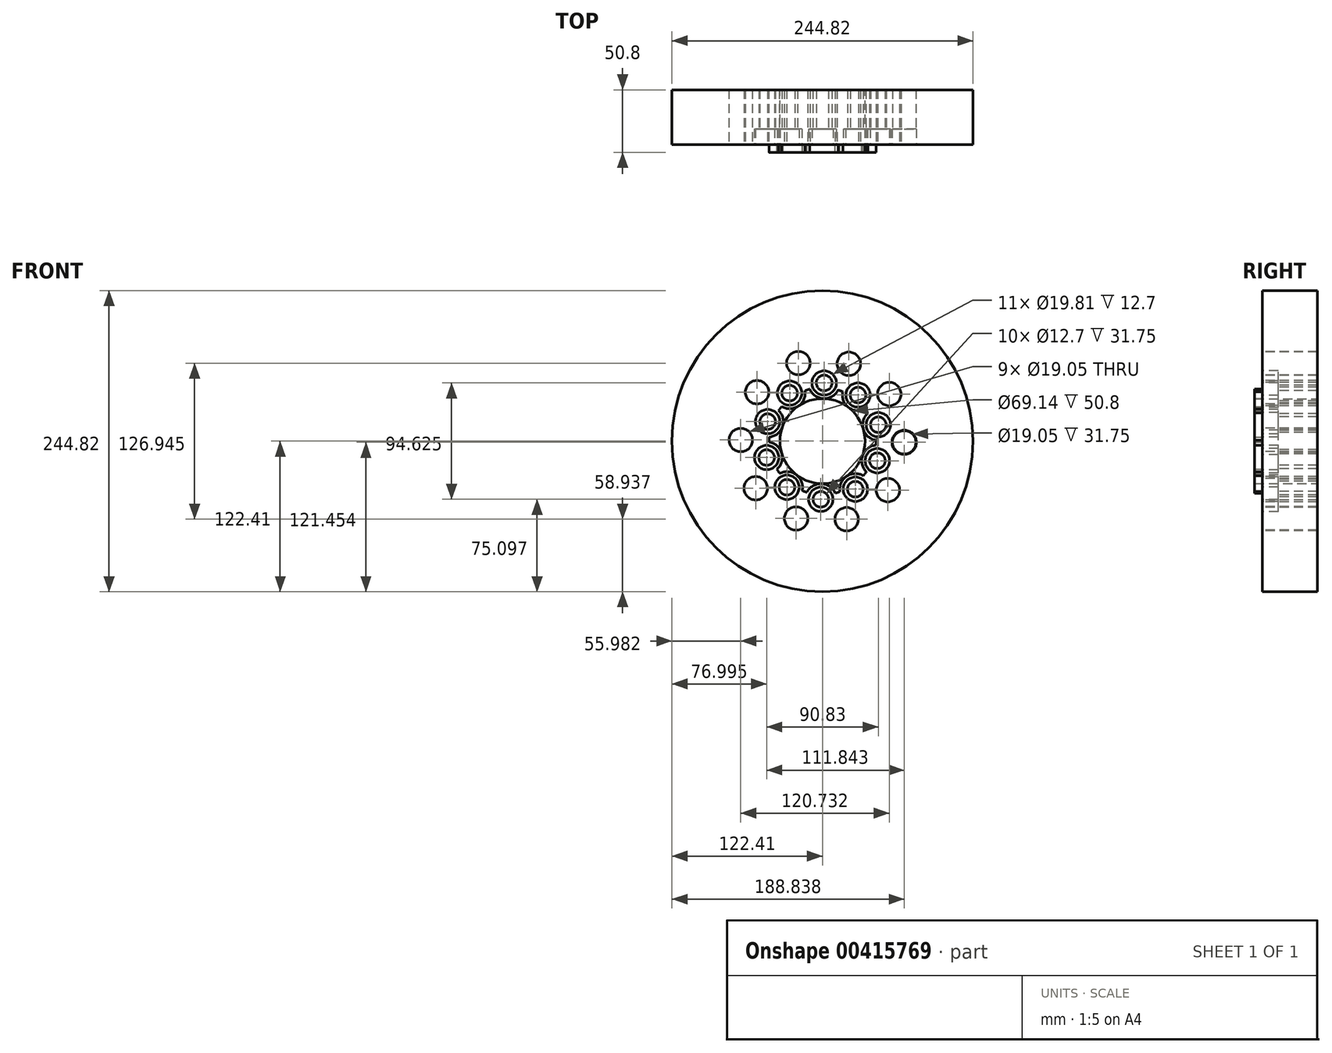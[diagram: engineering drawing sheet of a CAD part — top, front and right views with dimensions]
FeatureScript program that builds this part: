
annotation { "Feature Type Name" : "Feature", "Feature Type Description" : "" }
export const myFeature = defineFeature(function(context is Context, id is Id, definition is map)
    precondition{}
    {
        {
            var Q0;
            Q0=qCreatedBy(makeId("Front.planeOp"),FACE);
            var sketch = newSketch(context, id + "F0", { "sketchPlane" : qUnion([Q0])});
            skCircle(sketch, "E0", {"center": v(0, 0) * mm, "radius": 85.5 * mm});
            skCircle(sketch, "E1", {"center": v(0, 0) * mm, "radius": 43.5 * mm});
            skCircle(sketch, "E2", {"center": v(0, 0) * mm, "radius": 34.57 * mm});
            skCircle(sketch, "E3", {"center": v(0, 0) * mm, "radius": 122.4 * mm});
            skSolve(sketch);
        }
        {
            var Q0;
            Q0=makeQuery(id+"F0.imprint","IMPRINT",FACE,{"disambiguationData":[TD([[makeQuery(id+"F0.imprint","IMPRINT",EDGE,{"derivedFrom":sQuery(id+"F0.wireOp",EDGE,"E1")}),1.0]])]});
            extrude(context, id + "F1", {"entities" : qUnion([Q0]), "depth" : 50.8 * mm});
        }
        {
            var Q0;
            Q0=makeQuery(id+"F0.imprint","IMPRINT",FACE,{"disambiguationData":[TD([[makeQuery(id+"F0.imprint","IMPRINT",EDGE,{"derivedFrom":sQuery(id+"F0.wireOp",EDGE,"E0")}),1.0]])]});
            extrude(context, id + "F2", {"entities" : qUnion([Q0]), "operationType" : NewBodyOperationType.ADD, "depth" : 44.45 * mm});
        }
        {
            var Q0;
            Q0=makeQuery(id+"F2.opExtrude","CAP_FACE",FACE,{"disambiguationData":[OSD([sQuery(id+"F0.wireOp",EDGE,"E0"),sQuery(id+"F0.wireOp",EDGE,"E1")])],"isStart":false});
            var sketch = newSketch(context, id + "F3", { "sketchPlane" : qUnion([Q0])});
            skSolve(sketch);
        }
        {
            var Q0;
            Q0=makeQuery(id+"F3.imprint","IMPRINT",FACE,{"disambiguationData":[TD([[makeQuery(id+"F3.imprint","IMPRINT",EDGE,{"derivedFrom":makeQuery(id+"F2.opExtrude","CAP_EDGE",EDGE,{"disambiguationData":[OSD([sQuery(id+"F0.wireOp",EDGE,"E0")])],"isStart":false})}),1.0]])]});
            var sketch = newSketch(context, id + "F4", { "sketchPlane" : qUnion([Q0])});
            skPoint(sketch, "E4", {"position": v(21.44, 62.88) * mm});
            skPoint(sketch, "E5.1.0", {"position": v(-19.62, 63.47) * mm});
            skPoint(sketch, "E5.2.0", {"position": v(-53.18, 39.82) * mm});
            skPoint(sketch, "E5.3.0", {"position": v(-66.43, 0.96) * mm});
            skPoint(sketch, "E5.4.0", {"position": v(-54.3, -38.27) * mm});
            skPoint(sketch, "E5.5.0", {"position": v(-21.44, -62.88) * mm});
            skPoint(sketch, "E5.6.0", {"position": v(19.62, -63.47) * mm});
            skPoint(sketch, "E5.7.0", {"position": v(53.18, -39.82) * mm});
            skPoint(sketch, "E5.8.0", {"position": v(66.43, -0.96) * mm});
            skPoint(sketch, "E5.9.0", {"position": v(54.3, 38.27) * mm});
            skPoint(sketch, "E5.center", {"position": v(0, 0) * mm});
            skSolve(sketch);
        }
        {
            var Q0;
            Q0=sQuery(id+"F4.wireOp",VERTEX,"E5.1.0");
            var Q1;
            Q1=makeQuery(id+"F1.opExtrude","SWEPT_BODY",BODY,{"disambiguationData":[OSD([sQuery(id+"F0.wireOp",EDGE,"E1"),sQuery(id+"F0.wireOp",EDGE,"E2")])]});
            hole(context, id + "F5", {"style" : HoleStyle.SIMPLE, "endStyle" : HoleEndStyle.THROUGH, "holeDiameter" : 6.35 * mm, "isTappedThrough" : true, "tappedDepth" : 12.7 * mm, "tapClearance" : 3, "locations" : qUnion([Q0]), "scope" : qUnion([Q1])});
        }
        {
            var Q0;
            Q0=sQuery(id+"F4.wireOp",VERTEX,"E5.2.0");
            var Q1;
            Q1=makeQuery(id+"F1.opExtrude","SWEPT_BODY",BODY,{"disambiguationData":[OSD([sQuery(id+"F0.wireOp",EDGE,"E1"),sQuery(id+"F0.wireOp",EDGE,"E2")])]});
            hole(context, id + "F6", {"style" : HoleStyle.SIMPLE, "endStyle" : HoleEndStyle.THROUGH, "holeDiameter" : 6.35 * mm, "isTappedThrough" : true, "tappedDepth" : 12.7 * mm, "tapClearance" : 3, "locations" : qUnion([Q0]), "scope" : qUnion([Q1])});
        }
        {
            var Q0;
            Q0=sQuery(id+"F4.wireOp",VERTEX,"E5.3.0");
            var Q1;
            Q1=sQuery(id+"F4.wireOp",VERTEX,"E5.4.0");
            var Q2;
            Q2=sQuery(id+"F4.wireOp",VERTEX,"E5.5.0");
            var Q3;
            Q3=sQuery(id+"F4.wireOp",VERTEX,"E5.6.0");
            var Q4;
            Q4=sQuery(id+"F4.wireOp",VERTEX,"E5.7.0");
            var Q5;
            Q5=sQuery(id+"F4.wireOp",VERTEX,"E5.8.0");
            var Q6;
            Q6=sQuery(id+"F4.wireOp",VERTEX,"E5.9.0");
            var Q7;
            Q7=sQuery(id+"F4.wireOp",VERTEX,"E4");
            var Q8;
            Q8=makeQuery(id+"F1.opExtrude","SWEPT_BODY",BODY,{"disambiguationData":[OSD([sQuery(id+"F0.wireOp",EDGE,"E1"),sQuery(id+"F0.wireOp",EDGE,"E2")])]});
            hole(context, id + "F7", {"style" : HoleStyle.SIMPLE, "endStyle" : HoleEndStyle.THROUGH, "holeDiameter" : 6.35 * mm, "isTappedThrough" : true, "tappedDepth" : 12.7 * mm, "tapClearance" : 3, "locations" : qUnion([Q0, Q1, Q2, Q3, Q4, Q5, Q6, Q7]), "scope" : qUnion([Q8])});
        }
        {
            var Q0;
            Q0=makeQuery(id+"F4.imprint","IMPRINT",FACE,{"disambiguationData":[TD([[makeQuery(id+"F4.imprint","IMPRINT",EDGE,{"derivedFrom":makeQuery(id+"F3.imprint","IMPRINT",EDGE,{"derivedFrom":makeQuery(id+"F2.opExtrude","CAP_EDGE",EDGE,{"disambiguationData":[OSD([sQuery(id+"F0.wireOp",EDGE,"E0")])],"isStart":false})})}),1.0]])]});
            var sketch = newSketch(context, id + "F8", { "sketchPlane" : qUnion([Q0])});
            skPoint(sketch, "E6", {"position": v(28.9, 37.48) * mm});
            skPoint(sketch, "E7.1.0", {"position": v(1.35, 47.31) * mm});
            skPoint(sketch, "E7.2.0", {"position": v(-26.72, 39.07) * mm});
            skPoint(sketch, "E7.3.0", {"position": v(-44.58, 15.9) * mm});
            skPoint(sketch, "E7.4.0", {"position": v(-45.41, -13.33) * mm});
            skPoint(sketch, "E7.5.0", {"position": v(-28.9, -37.48) * mm});
            skPoint(sketch, "E7.6.0", {"position": v(-1.35, -47.31) * mm});
            skPoint(sketch, "E7.7.0", {"position": v(26.72, -39.07) * mm});
            skPoint(sketch, "E7.8.0", {"position": v(44.58, -15.9) * mm});
            skPoint(sketch, "E7.9.0", {"position": v(45.41, 13.33) * mm});
            skPoint(sketch, "E7.center", {"position": v(0, 0) * mm});
            skSolve(sketch);
        }
        {
            var Q0;
            Q0=sQuery(id+"F8.wireOp",VERTEX,"E7.3.0");
            var Q1;
            Q1=sQuery(id+"F8.wireOp",VERTEX,"E7.4.0");
            var Q2;
            Q2=sQuery(id+"F8.wireOp",VERTEX,"E7.5.0");
            var Q3;
            Q3=sQuery(id+"F8.wireOp",VERTEX,"E7.6.0");
            var Q4;
            Q4=sQuery(id+"F8.wireOp",VERTEX,"E7.7.0");
            var Q5;
            Q5=sQuery(id+"F8.wireOp",VERTEX,"E7.8.0");
            var Q6;
            Q6=sQuery(id+"F8.wireOp",VERTEX,"E7.9.0");
            var Q7;
            Q7=sQuery(id+"F8.wireOp",VERTEX,"E6");
            var Q8;
            Q8=sQuery(id+"F8.wireOp",VERTEX,"E7.1.0");
            var Q9;
            Q9=sQuery(id+"F8.wireOp",VERTEX,"E7.2.0");
            var Q10;
            Q10=makeQuery(id+"F1.opExtrude","SWEPT_BODY",BODY,{"disambiguationData":[OSD([sQuery(id+"F0.wireOp",EDGE,"E1"),sQuery(id+"F0.wireOp",EDGE,"E2")])]});
            hole(context, id + "F9", {"style" : HoleStyle.C_BORE, "endStyle" : HoleEndStyle.THROUGH, "oppositeDirection" : true, "holeDiameter" : 12.7 * mm, "cBoreDiameter" : 25.4 * mm, "cBoreDepth" : 12.7 * mm, "isTappedThrough" : true, "tappedDepth" : 12.7 * mm, "tapClearance" : 3, "locations" : qUnion([Q0, Q1, Q2, Q3, Q4, Q5, Q6, Q7, Q8, Q9]), "scope" : qUnion([Q10])});
        }
        {
            var Q0;
            Q0=sQuery(id+"F8.wireOp",VERTEX,"E7.2.0");
            var Q1;
            Q1=sQuery(id+"F8.wireOp",VERTEX,"E7.1.0");
            var Q2;
            Q2=sQuery(id+"F8.wireOp",VERTEX,"E6");
            var Q3;
            Q3=sQuery(id+"F8.wireOp",VERTEX,"E7.9.0");
            var Q4;
            Q4=sQuery(id+"F8.wireOp",VERTEX,"E7.8.0");
            var Q5;
            Q5=sQuery(id+"F8.wireOp",VERTEX,"E7.7.0");
            var Q6;
            Q6=sQuery(id+"F8.wireOp",VERTEX,"E7.6.0");
            var Q7;
            Q7=sQuery(id+"F8.wireOp",VERTEX,"E7.5.0");
            var Q8;
            Q8=sQuery(id+"F8.wireOp",VERTEX,"E7.4.0");
            var Q9;
            Q9=sQuery(id+"F8.wireOp",VERTEX,"E7.3.0");
            var Q10;
            Q10=sQuery(id+"F4.wireOp",VERTEX,"E5.8.0");
            var Q11;
            Q11=makeQuery(id+"F1.opExtrude","SWEPT_BODY",BODY,{"disambiguationData":[OSD([sQuery(id+"F0.wireOp",EDGE,"E1"),sQuery(id+"F0.wireOp",EDGE,"E2")])]});
            hole(context, id + "F10", {"style" : HoleStyle.C_BORE, "endStyle" : HoleEndStyle.THROUGH, "holeDiameter" : 12.7 * mm, "cBoreDiameter" : 19.8 * mm, "cBoreDepth" : 12.7 * mm, "isTappedThrough" : true, "tappedDepth" : 12.7 * mm, "tapClearance" : 3, "locations" : qUnion([Q0, Q1, Q2, Q3, Q4, Q5, Q6, Q7, Q8, Q9, Q10]), "scope" : qUnion([Q11])});
        }
        {
            var Q0;
            Q0=qCreatedBy(makeId("Front.planeOp"),FACE);
            var sketch = newSketch(context, id + "F11", { "sketchPlane" : qUnion([Q0])});
            skSolve(sketch);
        }
        {
            var Q0;
            Q0=sQuery(id+"F4.wireOp",VERTEX,"E5.3.0");
            var Q1;
            Q1=sQuery(id+"F4.wireOp",VERTEX,"E5.2.0");
            var Q2;
            Q2=sQuery(id+"F4.wireOp",VERTEX,"E5.1.0");
            var Q3;
            Q3=sQuery(id+"F4.wireOp",VERTEX,"E4");
            var Q4;
            Q4=sQuery(id+"F4.wireOp",VERTEX,"E5.9.0");
            var Q5;
            Q5=sQuery(id+"F4.wireOp",VERTEX,"E5.8.0");
            var Q6;
            Q6=sQuery(id+"F4.wireOp",VERTEX,"E5.7.0");
            var Q7;
            Q7=sQuery(id+"F4.wireOp",VERTEX,"E5.6.0");
            var Q8;
            Q8=sQuery(id+"F4.wireOp",VERTEX,"E5.5.0");
            var Q9;
            Q9=sQuery(id+"F4.wireOp",VERTEX,"E5.4.0");
            var Q10;
            Q10=makeQuery(id+"F1.opExtrude","SWEPT_BODY",BODY,{"disambiguationData":[OSD([sQuery(id+"F0.wireOp",EDGE,"E1"),sQuery(id+"F0.wireOp",EDGE,"E2")])]});
            hole(context, id + "F12", {"style" : HoleStyle.SIMPLE, "endStyle" : HoleEndStyle.THROUGH, "holeDiameter" : 19.05 * mm, "isTappedThrough" : true, "tappedDepth" : 12.7 * mm, "tapClearance" : 3, "locations" : qUnion([Q0, Q1, Q2, Q3, Q4, Q5, Q6, Q7, Q8, Q9]), "scope" : qUnion([Q10])});
        }
        {
            var Q0;
            Q0=makeQuery(id+"F0.imprint","IMPRINT",FACE,{"disambiguationData":[TD([[makeQuery(id+"F0.imprint","IMPRINT",EDGE,{"derivedFrom":sQuery(id+"F0.wireOp",EDGE,"E0")}),-1.0]])]});
            extrude(context, id + "F13", {"entities" : qUnion([Q0]), "operationType" : NewBodyOperationType.ADD, "depth" : 44.45 * mm});
        }
    });
